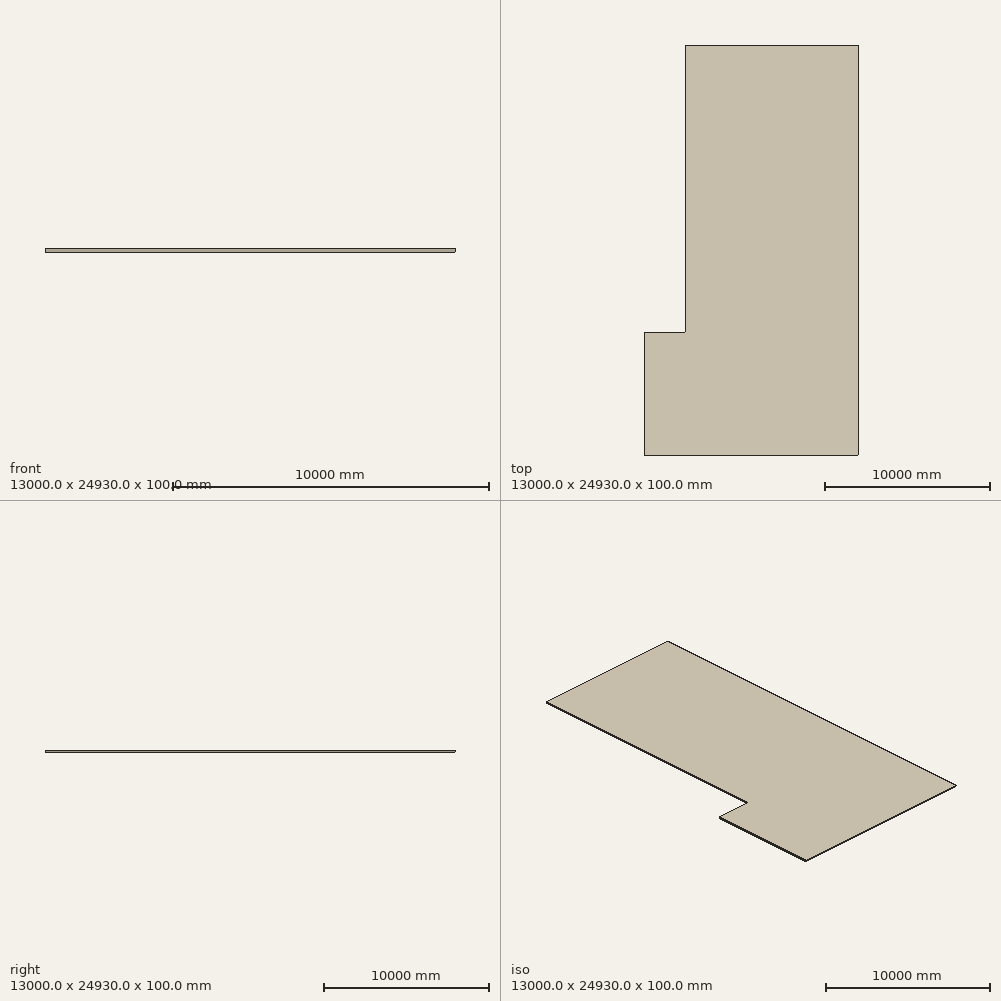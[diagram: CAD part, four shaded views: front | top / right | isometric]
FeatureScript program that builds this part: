
annotation { "Feature Type Name" : "Feature", "Feature Type Description" : "" }
export const myFeature = defineFeature(function(context is Context, id is Id, definition is map)
    precondition{}
    {
        {
            var Q0;
            Q0=qCreatedBy(makeId("Top.planeOp"),FACE);
            var sketch = newSketch(context, id + "F0", { "sketchPlane" : qUnion([Q0])});
            skLineSegment(sketch, "E0", {"start": v(0, 0) * mm, "end": v(13000, 0) * mm});
            skLineSegment(sketch, "E1", {"start": v(13000, 0) * mm, "end": v(13000, 24930) * mm});
            skLineSegment(sketch, "E2", {"start": v(13000, 24930) * mm, "end": v(2500, 24930) * mm});
            skLineSegment(sketch, "E3", {"start": v(2500, 24930) * mm, "end": v(2500, 7500) * mm});
            skLineSegment(sketch, "E4", {"start": v(2500, 7500) * mm, "end": v(0, 7500) * mm});
            skLineSegment(sketch, "E5", {"start": v(0, 7500) * mm, "end": v(0, 0) * mm});
            skSolve(sketch);
        }
        {
            var Q0;
            Q0 = qSketchRegion(id + "F0", true);
            extrude(context, id + "F1", {"entities" : qUnion([Q0]), "depth" : 100 * mm});
        }
    });
